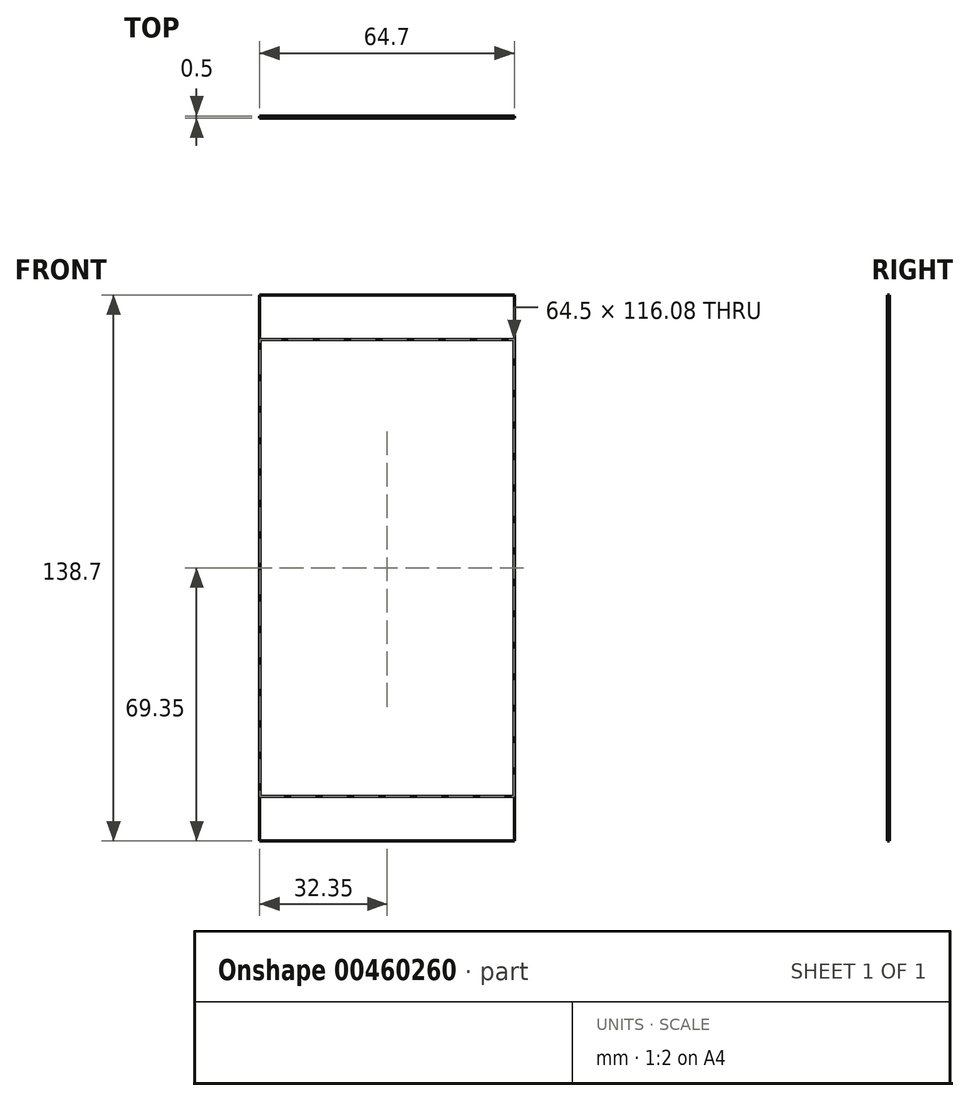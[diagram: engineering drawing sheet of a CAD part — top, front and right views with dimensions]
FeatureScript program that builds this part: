
annotation { "Feature Type Name" : "Feature", "Feature Type Description" : "" }
export const myFeature = defineFeature(function(context is Context, id is Id, definition is map)
    precondition{}
    {
        {
            var Q0;
            Q0=qCreatedBy(makeId("Front.planeOp"),FACE);
            var sketch = newSketch(context, id + "F0", { "sketchPlane" : qUnion([Q0])});
            skLineSegment(sketch, "E0", {"start": v(-32.35, 69.35) * mm, "end": v(32.35, 69.35) * mm});
            skLineSegment(sketch, "E1", {"start": v(32.35, 69.35) * mm, "end": v(32.35, -69.35) * mm});
            skLineSegment(sketch, "E2", {"start": v(32.35, -69.35) * mm, "end": v(-32.35, -69.35) * mm});
            skLineSegment(sketch, "E3", {"start": v(-32.35, -69.35) * mm, "end": v(-32.35, 69.35) * mm});
            skSolve(sketch);
        }
        {
            var Q0;
            Q0 = qSketchRegion(id + "F0", true);
            extrude(context, id + "F1", {"entities" : qUnion([Q0]), "depth" : 2 * mm});
        }
        {
            var Q0;
            Q0=makeQuery(id+"F1.opExtrude","CAP_FACE",FACE,{"disambiguationData":[OSD([sQuery(id+"F0.wireOp",EDGE,"E0"),sQuery(id+"F0.wireOp",EDGE,"E1"),sQuery(id+"F0.wireOp",EDGE,"E2"),sQuery(id+"F0.wireOp",EDGE,"E3")])],"isStart":true});
            extrude(context, id + "F2", {"entities" : qUnion([Q0]), "operationType" : NewBodyOperationType.REMOVE, "oppositeDirection" : true, "depth" : 1.5 * mm});
        }
        {
            var Q0;
            Q0=qCreatedBy(makeId("Front.planeOp"),FACE);
            var sketch = newSketch(context, id + "F3", { "sketchPlane" : qUnion([Q0])});
            skLineSegment(sketch, "E4.bottom", {"start": v(32.25, -58.04) * mm, "end": v(-32.25, -58.04) * mm});
            skLineSegment(sketch, "E4.top", {"start": v(32.25, 58.04) * mm, "end": v(-32.25, 58.04) * mm});
            skLineSegment(sketch, "E4.left", {"start": v(32.25, -58.04) * mm, "end": v(32.25, 58.04) * mm});
            skLineSegment(sketch, "E4.right", {"start": v(-32.25, -58.04) * mm, "end": v(-32.25, 58.04) * mm});
            skSolve(sketch);
        }
        {
            var Q0;
            Q0 = qSketchRegion(id + "F3", true);
            extrude(context, id + "F4", {"entities" : qUnion([Q0]), "operationType" : NewBodyOperationType.REMOVE, "depth" : 43.24 * mm});
        }
    });
